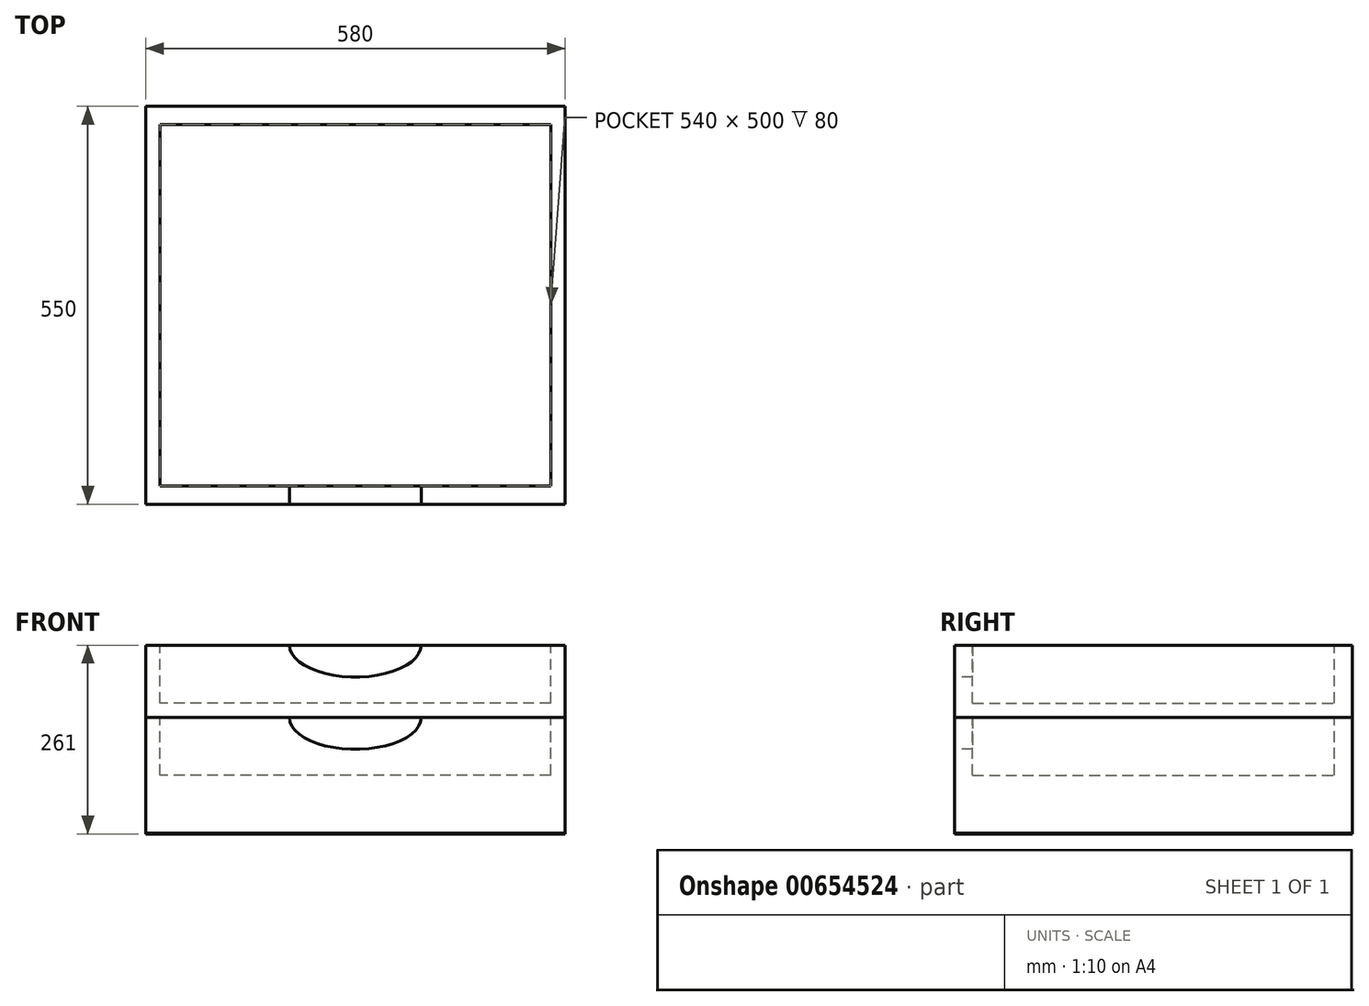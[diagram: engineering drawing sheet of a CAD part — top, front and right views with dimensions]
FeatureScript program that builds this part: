
annotation { "Feature Type Name" : "Feature", "Feature Type Description" : "" }
export const myFeature = defineFeature(function(context is Context, id is Id, definition is map)
    precondition{}
    {
        {
            var Q0;
            Q0=qCreatedBy(makeId("Top.planeOp"),FACE);
            var sketch = newSketch(context, id + "F0", { "sketchPlane" : qUnion([Q0])});
            skLineSegment(sketch, "E0.bottom", {"start": v(290, -275) * mm, "end": v(-290, -275) * mm});
            skLineSegment(sketch, "E0.top", {"start": v(290, 275) * mm, "end": v(-290, 275) * mm});
            skLineSegment(sketch, "E0.left", {"start": v(290, -275) * mm, "end": v(290, 275) * mm});
            skLineSegment(sketch, "E0.right", {"start": v(-290, -275) * mm, "end": v(-290, 275) * mm});
            skPoint(sketch, "E0.middle", {"position": v(0, 0) * mm});
            skSolve(sketch);
        }
        {
            var Q0;
            Q0 = qSketchRegion(id + "F0", true);
            extrude(context, id + "F1", {"entities" : qUnion([Q0]), "depth" : 1 * mm, "offsetDistance" : 25 * mm});
        }
        {
            var Q0;
            Q0=makeQuery(id+"F1.opExtrude","CAP_FACE",FACE,{"disambiguationData":[OSD([sQuery(id+"F0.wireOp",EDGE,"E0.bottom"),sQuery(id+"F0.wireOp",EDGE,"E0.top"),sQuery(id+"F0.wireOp",EDGE,"E0.left"),sQuery(id+"F0.wireOp",EDGE,"E0.right")])],"isStart":false});
            var sketch = newSketch(context, id + "F2", { "sketchPlane" : qUnion([Q0])});
            skSolve(sketch);
        }
        {
            var Q0;
            Q0=makeQuery(id+"F2.imprint","IMPRINT",FACE,{"disambiguationData":[TD([[makeQuery(id+"F2.imprint","IMPRINT",EDGE,{"derivedFrom":makeQuery(id+"F1.opExtrude","CAP_EDGE",EDGE,{"disambiguationData":[OSD([sQuery(id+"F0.wireOp",EDGE,"E0.bottom")])],"isStart":false})}),-1.0]])]});
            extrude(context, id + "F3", {"entities" : qUnion([Q0]), "depth" : 160 * mm, "offsetDistance" : 25 * mm});
        }
        {
            var Q0;
            Q0=makeQuery(id+"F3.opExtrude","SWEPT_FACE",FACE,{"disambiguationData":[OSD([sQuery(id+"F0.wireOp",EDGE,"E0.bottom")])]});
            var sketch = newSketch(context, id + "F4", { "sketchPlane" : qUnion([Q0])});
            skEllipse(sketch, "E1", {"center": v(0, 161) * mm, "majorRadius": 91.04 * mm, "minorRadius": 44.02 * mm, "majorAxis": v(1, 0)});
            skSolve(sketch);
        }
        {
            var Q0;
            Q0 = qSketchRegion(id + "F4", true);
            extrude(context, id + "F5", {"entities" : qUnion([Q0]), "operationType" : NewBodyOperationType.REMOVE, "oppositeDirection" : true, "depth" : 25 * mm, "offsetDistance" : 25 * mm});
        }
        {
            var Q0;
            Q0=makeQuery(id+"F3.opExtrude","CAP_FACE",FACE,{"disambiguationData":[OSD([sQuery(id+"F0.wireOp",EDGE,"E0.bottom"),sQuery(id+"F0.wireOp",EDGE,"E0.top"),sQuery(id+"F0.wireOp",EDGE,"E0.left"),sQuery(id+"F0.wireOp",EDGE,"E0.right")])],"isStart":false});
            var sketch = newSketch(context, id + "F6", { "sketchPlane" : qUnion([Q0])});
            skLineSegment(sketch, "E2.bottom", {"start": v(270, -250) * mm, "end": v(-270, -250) * mm});
            skLineSegment(sketch, "E2.top", {"start": v(270, 250) * mm, "end": v(-270, 250) * mm});
            skLineSegment(sketch, "E2.left", {"start": v(270, -250) * mm, "end": v(270, 250) * mm});
            skLineSegment(sketch, "E2.right", {"start": v(-270, -250) * mm, "end": v(-270, 250) * mm});
            skPoint(sketch, "E2.middle", {"position": v(0, 0) * mm});
            skSolve(sketch);
        }
        {
            var Q0;
            Q0 = qSketchRegion(id + "F6", true);
            extrude(context, id + "F7", {"entities" : qUnion([Q0]), "operationType" : NewBodyOperationType.REMOVE, "oppositeDirection" : true, "depth" : 80 * mm, "offsetDistance" : 25 * mm});
        }
        {
            var Q0;
            Q0=makeQuery(id+"F3.opExtrude","CAP_FACE",FACE,{"disambiguationData":[OSD([sQuery(id+"F0.wireOp",EDGE,"E0.bottom"),sQuery(id+"F0.wireOp",EDGE,"E0.top"),sQuery(id+"F0.wireOp",EDGE,"E0.left"),sQuery(id+"F0.wireOp",EDGE,"E0.right")])],"isStart":false});
            var sketch = newSketch(context, id + "F8", { "sketchPlane" : qUnion([Q0])});
            skLineSegment(sketch, "E3.bottom", {"start": v(290, -275) * mm, "end": v(-290, -275) * mm});
            skLineSegment(sketch, "E3.top", {"start": v(290, 275) * mm, "end": v(-290, 275) * mm});
            skLineSegment(sketch, "E3.left", {"start": v(290, -275) * mm, "end": v(290, 275) * mm});
            skLineSegment(sketch, "E3.right", {"start": v(-290, -275) * mm, "end": v(-290, 275) * mm});
            skPoint(sketch, "E3.middle", {"position": v(0, 0) * mm});
            skSolve(sketch);
        }
        {
            var Q0;
            Q0 = qSketchRegion(id + "F8", true);
            extrude(context, id + "F9", {"entities" : qUnion([Q0]), "depth" : 100 * mm, "offsetDistance" : 25 * mm});
        }
        {
            var Q0;
            Q0=makeQuery(id+"F9.opExtrude","SWEPT_FACE",FACE,{"disambiguationData":[OSD([sQuery(id+"F8.wireOp",EDGE,"E3.bottom")])]});
            var sketch = newSketch(context, id + "F10", { "sketchPlane" : qUnion([Q0])});
            skEllipse(sketch, "E4", {"center": v(0, 261) * mm, "majorRadius": 91.04 * mm, "minorRadius": 44.02 * mm, "majorAxis": v(1, 0)});
            skSolve(sketch);
        }
        {
            var Q0;
            Q0 = qSketchRegion(id + "F10", true);
            extrude(context, id + "F11", {"entities" : qUnion([Q0]), "operationType" : NewBodyOperationType.REMOVE, "oppositeDirection" : true, "depth" : 25 * mm, "offsetDistance" : 25 * mm});
        }
        {
            var Q0;
            Q0=makeQuery(id+"F9.opExtrude","CAP_FACE",FACE,{"disambiguationData":[OSD([sQuery(id+"F8.wireOp",EDGE,"E3.bottom"),sQuery(id+"F8.wireOp",EDGE,"E3.top"),sQuery(id+"F8.wireOp",EDGE,"E3.left"),sQuery(id+"F8.wireOp",EDGE,"E3.right")])],"isStart":false});
            var sketch = newSketch(context, id + "F12", { "sketchPlane" : qUnion([Q0])});
            skLineSegment(sketch, "E5.bottom", {"start": v(270, -250) * mm, "end": v(-270, -250) * mm});
            skLineSegment(sketch, "E5.top", {"start": v(270, 250) * mm, "end": v(-270, 250) * mm});
            skLineSegment(sketch, "E5.left", {"start": v(270, -250) * mm, "end": v(270, 250) * mm});
            skLineSegment(sketch, "E5.right", {"start": v(-270, -250) * mm, "end": v(-270, 250) * mm});
            skPoint(sketch, "E5.middle", {"position": v(0, 0) * mm});
            skSolve(sketch);
        }
        {
            var Q0;
            Q0 = qSketchRegion(id + "F12", true);
            extrude(context, id + "F13", {"entities" : qUnion([Q0]), "operationType" : NewBodyOperationType.REMOVE, "oppositeDirection" : true, "depth" : 80 * mm, "offsetDistance" : 25 * mm});
        }
    });
